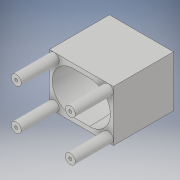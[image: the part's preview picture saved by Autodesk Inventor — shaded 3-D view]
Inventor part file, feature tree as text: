
AUTODESK INVENTOR PART (.ipt)
format: ipt  version: 2019 (Build 230136000, 136)  size: 277,504 bytes
history: native  units: mm
features: sketch x6, projected_geometry x4, extrude x2, hole x2, plane x1, loft x1, other x1
ambient origin geometry x8: Origin, YZ Plane, XZ Plane, XY Plane, X Axis, Y Axis, Z Axis, Center Point
bodies: Solid1 (feature_tree)
feature tree (17):
  extrude  "Extrusion1"  Depth=64.0mm
  sketch  "Sketch2"  dims[d2=18.0mm d3=16.0mm]
  plane  "Work Plane1"
  loft  "Loft1"
  hole  "Hole1"  [1 undecoded]
  extrude  "Extrusion2"  Depth=16.0mm
  hole  "Hole3"  [1 undecoded]
  sketch  "Sketch1"  dims[d0=64.0mm d1=51.0mm]
  sketch  "Sketch3"  dims[d4=10.0mm d5=60.0mm d6=0.0mm]
  other  "Edges1"
  sketch  "Sketch4"  dims[d7=42.0mm d9=16.0mm]
  sketch  "Sketch6"  dims[d10=-30.0mm d11=14.0mm]
  sketch  "Sketch7"  dims[d12=40.0mm d13=0.0mm d14=90.0deg d15=0.0mm d16=90.0deg d17=0.0mm d18=90.0deg d20=12.0mm d21=15.0mm d22=13.0mm d23=16.0mm d24=10.0mm d25=15.0mm d26=10.0mm d27=3.0mm d28=6.0mm d29=4.0mm d30=2.0mm d31=90.0deg d32=6.0mm d33=20.594885mm d45=10.0mm d46=5.0mm d47=5.0mm d48=5.0mm d49=5.0mm d50=10.0mm d51=10.0mm d52=10.0mm d53=38.0mm d54=0.0mm d55=3.0mm d56=6.0mm d57=4.0mm d58=2.0mm d59=90.0deg d60=20.0mm d61=0.0mm]
  projected_geometry  "Projected Loop1"
  projected_geometry  "Projected Loop2"
  projected_geometry  "Projected Loop3"
  projected_geometry  "Projected Loop4"
note: 2 required parameter values undecoded (feature->parameter linkage not recoverable at this tier; creation-order binding heuristic only, values carry confidence <= 0.55)
